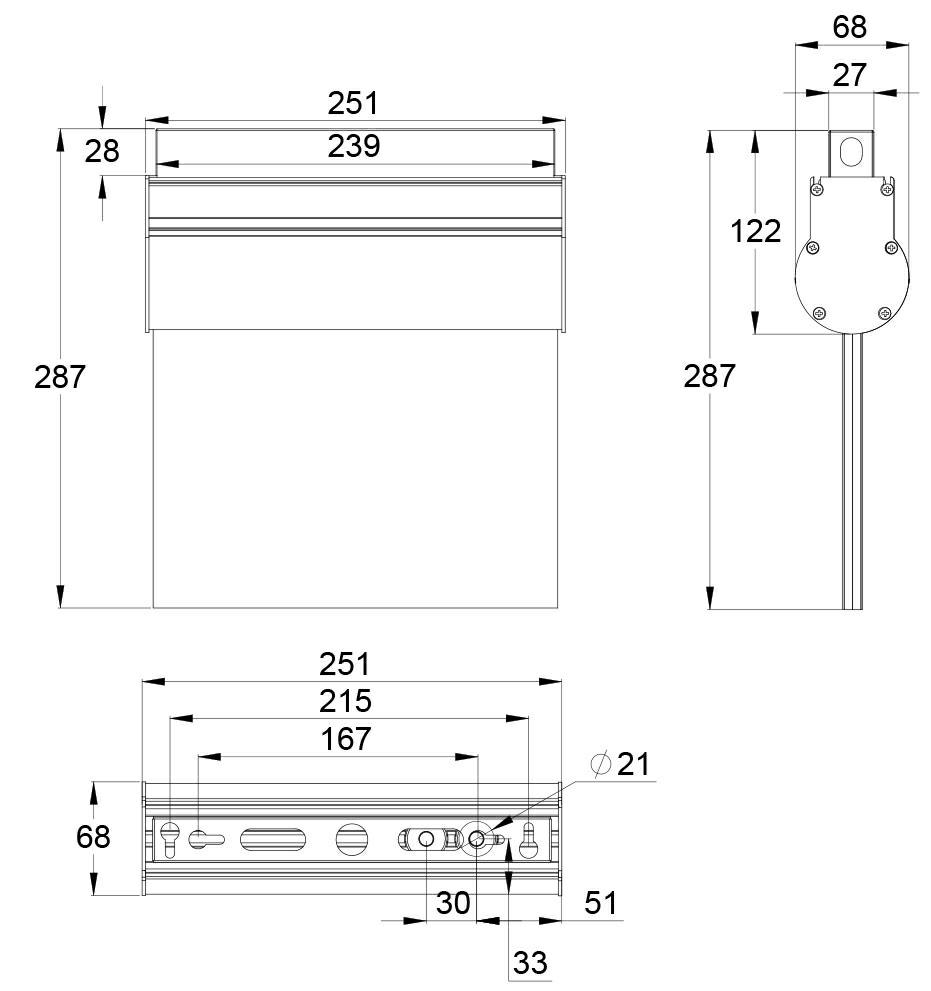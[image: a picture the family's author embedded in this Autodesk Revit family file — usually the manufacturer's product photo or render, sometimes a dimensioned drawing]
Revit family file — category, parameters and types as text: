
# Revit family: ESC 10 LED EMERGENCY EXIT LIGHT TW84451W
name_source: partatom
category: Electrical Fixtures
revit_build: Autodesk Revit 2015 (Build: 20160512_0715(x64)
units: mm (PartAtom-declared; Revit-internal decimal feet)

## types (3) — shared parameters
Depth = 95 mm  [stored 0.31168 ft]
Height = 219 mm  [stored 0.718504 ft]
Manufacturer = Teknoware Oy
Model = ESC 10 TW844
Product Code = TW84451W
Viewing Distance = 30000 mm
Width = 277 mm  [stored 0.908793 ft]

## per-type parameters (varying)
| type | Back Pictogram | Down | Front Pictogram | Left | Right | Type Comments |
| -arrow right | Teknoware Pictogram PBV10301E left | No | Teknoware Pictogram PBV10301E right | No | Yes | PBV10301E |
| -arrow left | Teknoware Pictogram PBV10301E right | No | Teknoware Pictogram PBV10301E left | Yes | No | PBV10301E |
| -arrow down | Teknoware Pictogram PBV10302E | Yes | Teknoware Pictogram PBV10302E | No | No | PBV10302E |

note: [stored X ft] marks values corroborated as IEEE doubles in the binary element streams (Revit-internal decimal feet)

## geometry (parser evidence)
native form markers: Blend x2, Sweep x12
no freeform markers — native parametric forms only
